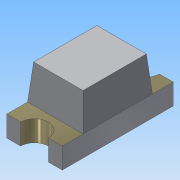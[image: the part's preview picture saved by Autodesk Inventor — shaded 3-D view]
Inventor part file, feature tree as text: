
AUTODESK INVENTOR PART (.ipt)
format: ipt  version: 2016 (Build 200138000, 138)  size: 136,192 bytes
history: native  units: mm
features: extrude x4, sketch x2, projected_geometry x1
ambient origin geometry x8: Origin, YZ Plane, XZ Plane, XY Plane, X Axis, Y Axis, Z Axis, Center Point
bodies: Body1 (feature_tree)
feature tree (7):
  extrude  "Extrusion4"  Depth=0.8mm
  sketch  "Sketch11"  dims[d9=0.2mm d10=0.3mm d11=0.0mm d12=1.0mm d13=0.8mm d14=0.5mm d15=-0.872665mm d16=0.3mm d17=0.1mm d18=0.0mm d20=0.15mm d21=0.1mm d22=0.1mm d23=0.01mm d24=0.0mm]
  extrude  "Extrusion6"  Depth=0.3mm TaperAngle=0.0deg
  extrude  "Extrusion5"  Depth=0.01mm
  extrude  "Extrusion7"  Depth=0.8mm
  sketch  "Sketch10"  dims[d7=1.6mm d8=0.8mm]
  projected_geometry  "Projected Loop1"
